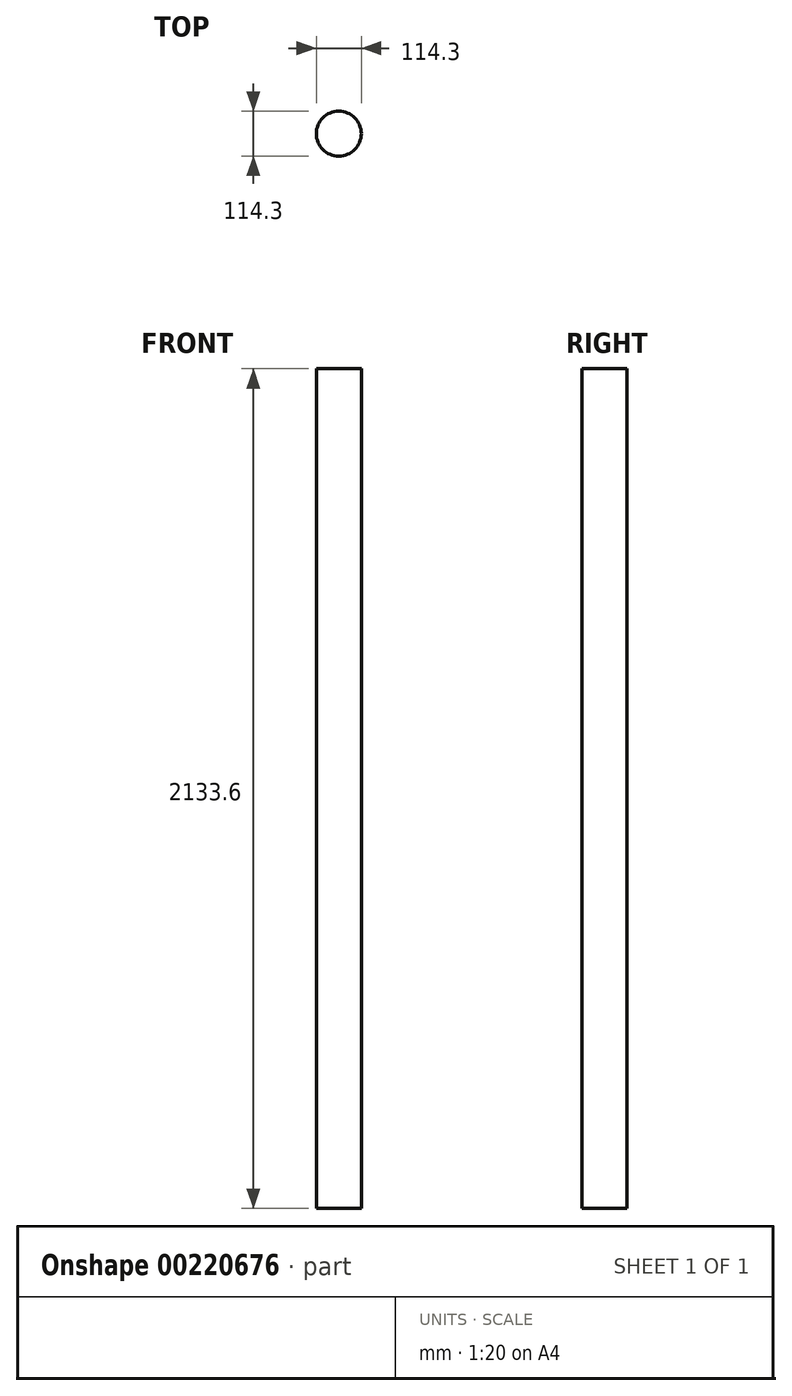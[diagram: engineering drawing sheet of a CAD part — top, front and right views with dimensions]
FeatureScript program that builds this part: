
annotation { "Feature Type Name" : "Feature", "Feature Type Description" : "" }
export const myFeature = defineFeature(function(context is Context, id is Id, definition is map)
    precondition{}
    {
        {
            var Q0;
            Q0=qCreatedBy(makeId("Top.planeOp"),FACE);
            var sketch = newSketch(context, id + "F0", { "sketchPlane" : qUnion([Q0])});
            skCircle(sketch, "E0", {"center": v(0, 0) * mm, "radius": 57.15 * mm});
            skSolve(sketch);
        }
        {
            var Q0;
            Q0 = qSketchRegion(id + "F0", true);
            extrude(context, id + "F1", {"entities" : qUnion([Q0]), "depth" : 2133.6 * mm});
        }
    });
